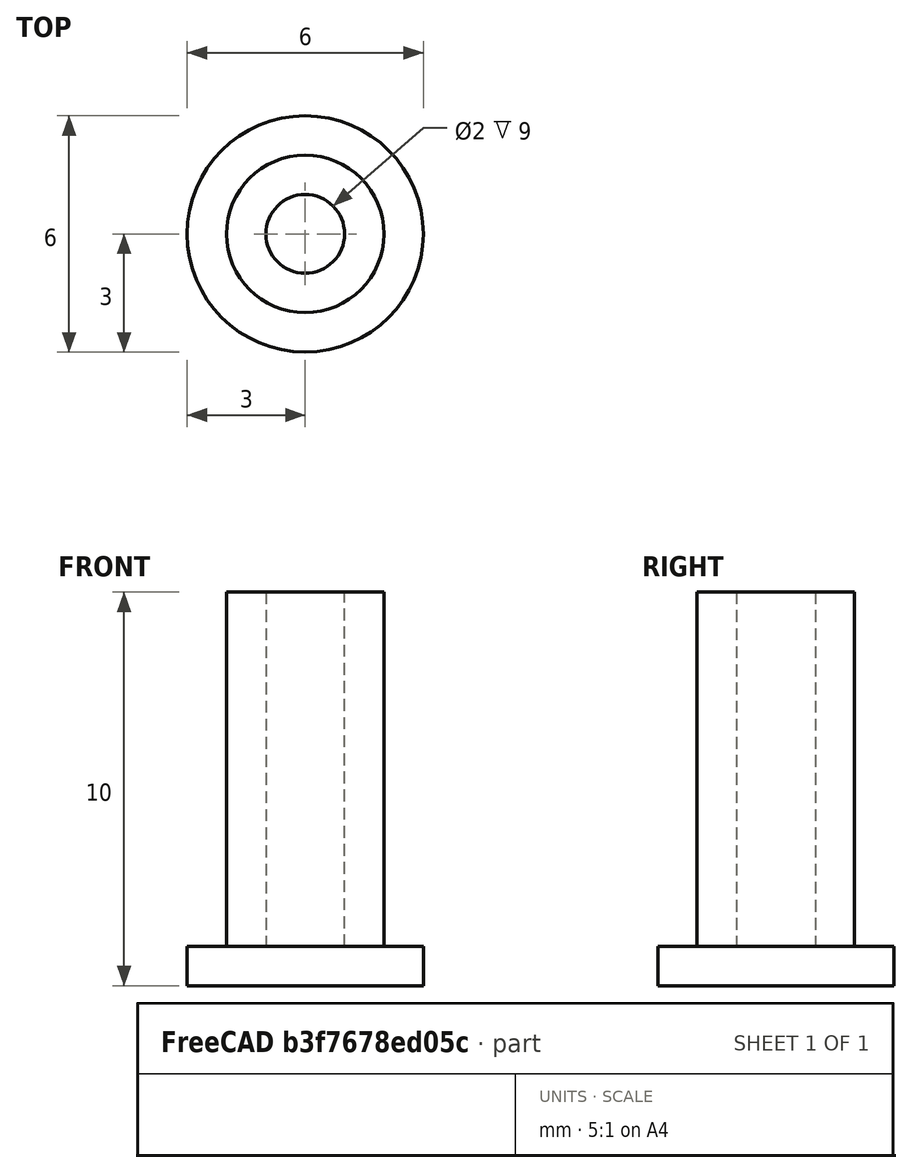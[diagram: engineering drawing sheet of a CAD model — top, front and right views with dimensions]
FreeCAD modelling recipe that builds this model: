
FCSTD DOCUMENT  (FreeCAD 0.19R24291 (Git))
Label: anti-flex
License: All rights reserved
LicenseURL: http://en.wikipedia.org/wiki/All_rights_reserved
objects: Part::Part2DObjectPython×3, Part::Extrusion×3, Part::Cut×1, Part::MultiFuse×1
note: 8 computed .brp shape members not serialized (recipe doc carries the construction recipe); baked Part::Feature solids carry a one-line shape summary decoded from their .brp

FEATURE [Part::Part2DObjectPython] Circle  label="inner"  # Draft 2D object (typed FeaturePython)
  Area = 0
  FirstAngle = 0
  LastAngle = 0
  MakeFace = false
  Radius = 1
FEATURE [Part::Part2DObjectPython] Circle001  label="outer"  # Draft 2D object (typed FeaturePython)
  Area = 0
  FirstAngle = 0
  LastAngle = 0
  MakeFace = false
  Radius = 2
FEATURE [Part::Part2DObjectPython] Circle002  label="foot"  # Draft 2D object (typed FeaturePython)
  Area = 0
  FirstAngle = 0
  LastAngle = 0
  MakeFace = false
  Radius = 3
FEATURE [Part::Extrusion] Extrude  label="ext_inner"
  Base = -> Circle
  Dir = (0,0,1)
  DirMode = 2
  FaceMakerClass = Part::FaceMakerBullseye
  LengthFwd = 11
  LengthRev = 0
  Solid = true
  Symmetric = false
FEATURE [Part::Extrusion] Extrude001  label="ext_outer"
  Base = -> Circle001
  Dir = (0,0,1)
  DirMode = 2
  FaceMakerClass = Part::FaceMakerBullseye
  LengthFwd = 10
  LengthRev = 0
  Solid = true
  Symmetric = false
FEATURE [Part::Cut] Cut  label="outer_min_inner"
  Base = -> Extrude001
  Tool = -> Extrude
FEATURE [Part::Extrusion] Extrude002  label="ext_foot"
  Base = -> Circle002
  Dir = (0,0,1)
  DirMode = 2
  FaceMakerClass = Part::FaceMakerBullseye
  LengthFwd = 1
  LengthRev = 0
  Solid = true
  Symmetric = false
FEATURE [Part::MultiFuse] Fusion  label="anti-flex"
  Shapes = -> [Cut,Extrude002]
